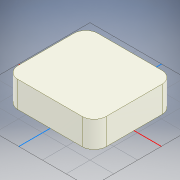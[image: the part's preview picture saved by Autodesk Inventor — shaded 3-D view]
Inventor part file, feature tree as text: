
AUTODESK INVENTOR PART (.ipt)
format: ipt  version: 2022 (Build 260153000, 153)  size: 106,496 bytes
history: native  units: mm
features: other x1, extrude x1, fillet x1, sketch x1
ambient origin geometry x8: Origin, YZ Plane, XZ Plane, XY Plane, X Axis, Y Axis, Z Axis, Center Point
bodies: Body1 (feature_tree)
feature tree (4):
  other  "Твердое тело1"
  extrude  "Выдавливание1"  Depth=74.0mm
  fillet  "Сопряжение1"  Radius=67.0mm
  sketch  "Эскиз1"
